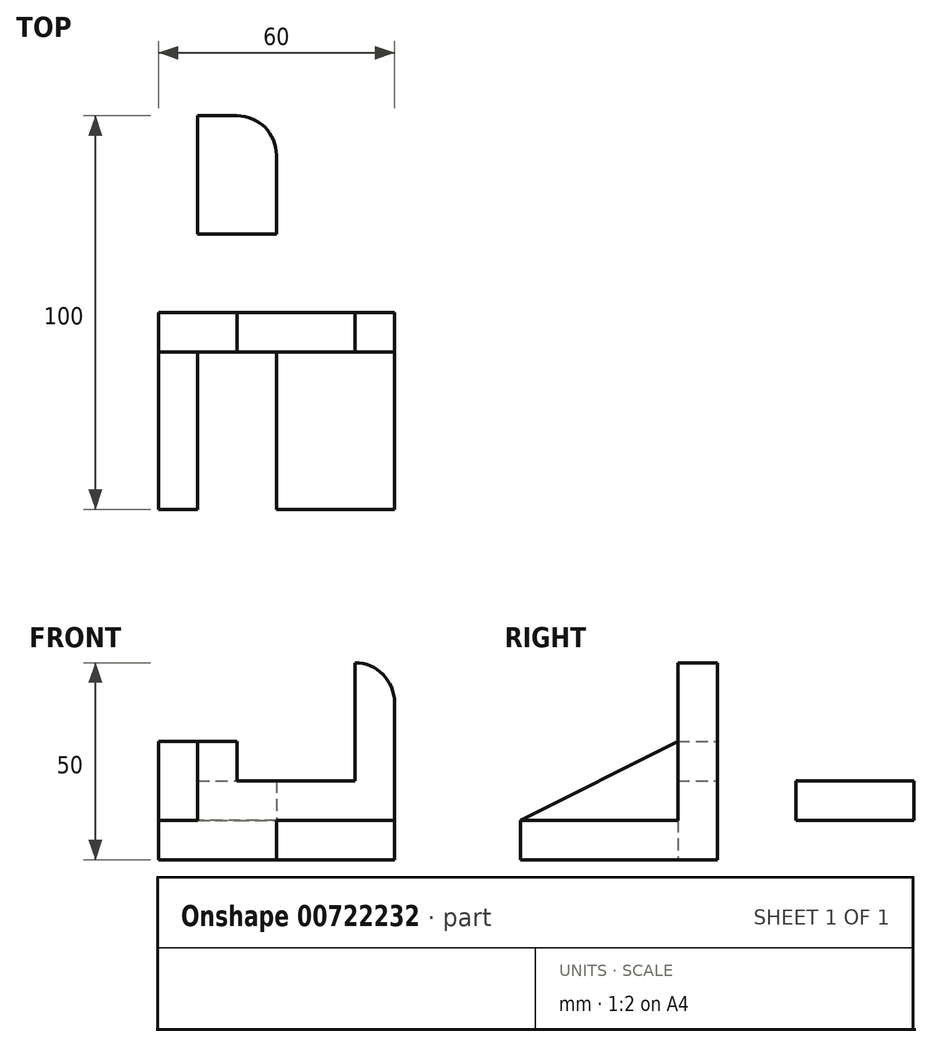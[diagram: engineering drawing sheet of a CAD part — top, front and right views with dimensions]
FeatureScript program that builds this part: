
annotation { "Feature Type Name" : "Feature", "Feature Type Description" : "" }
export const myFeature = defineFeature(function(context is Context, id is Id, definition is map)
    precondition{}
    {
        {
            var Q0;
            Q0=qCreatedBy(makeId("Front.planeOp"),FACE);
            var sketch = newSketch(context, id + "F0", { "sketchPlane" : qUnion([Q0])});
            skLineSegment(sketch, "E0", {"start": v(0, 0) * mm, "end": v(60, 0) * mm});
            skLineSegment(sketch, "E1", {"start": v(0, 0) * mm, "end": v(0, 10) * mm});
            skLineSegment(sketch, "E2", {"start": v(30, 0) * mm, "end": v(60, 0) * mm});
            skLineSegment(sketch, "E3", {"start": v(60, 10) * mm, "end": v(60, 0) * mm});
            skLineSegment(sketch, "E4", {"start": v(0, 10) * mm, "end": v(60, 10) * mm});
            skLineSegment(sketch, "E5", {"start": v(30, 10) * mm, "end": v(30, 0) * mm});
            skLineSegment(sketch, "E6", {"start": v(0, 30) * mm, "end": v(0, 10) * mm});
            skLineSegment(sketch, "E7", {"start": v(0, 30) * mm, "end": v(10, 30) * mm});
            skLineSegment(sketch, "E8", {"start": v(10, 10) * mm, "end": v(10, 30) * mm});
            skLineSegment(sketch, "E9", {"start": v(20, 30) * mm, "end": v(10, 30) * mm});
            skLineSegment(sketch, "E10", {"start": v(20, 20) * mm, "end": v(20, 30) * mm});
            skLineSegment(sketch, "E11", {"start": v(20, 20) * mm, "end": v(50, 20) * mm});
            skLineSegment(sketch, "E12", {"start": v(60, 40) * mm, "end": v(60, 10) * mm});
            skLineSegment(sketch, "E13", {"start": v(50, 50) * mm, "end": v(50, 50) * mm});
            skLineSegment(sketch, "E14", {"start": v(50, 20) * mm, "end": v(50, 50) * mm});
            skPoint(sketch, "E15.visualSharp", {"position": v(60, 50) * mm});
            skArc(sketch, "E15.filletArc", {"start": v(60, 40) * mm, "mid": v(57.07, 47.07) * mm, "end": v(50, 50) * mm});
            skSolve(sketch);
        }
        {
            var Q0;
            {var subQ0=sQuery(id+"F0.wireOp",EDGE,"E6");Q0=makeQuery(id+"F0.imprint","IMPRINT",FACE,{"disambiguationData":[TD([[makeQuery(id+"F0.imprint","IMPRINT",EDGE,{"derivedFrom":subQ0}),1.0]])]});}
            var Q1;
            Q1=makeQuery(id+"F0.imprint","IMPRINT",FACE,{"disambiguationData":[TD([[makeQuery(id+"F0.imprint","IMPRINT",EDGE,{"derivedFrom":sQuery(id+"F0.wireOp",EDGE,"E0")}),1.0]])]});
            extrude(context, id + "F1", {"entities" : qUnion([Q0, Q1]), "depth" : 50 * mm, "offsetDistance" : 25 * mm});
        }
        {
            var Q0;
            Q0 = qSketchRegion(id + "F0", true);
            extrude(context, id + "F2", {"entities" : qUnion([Q0]), "operationType" : NewBodyOperationType.ADD, "depth" : 10 * mm, "offsetDistance" : 25 * mm});
        }
        {
            var Q0;
            Q0=makeQuery(id+"F2.opExtrude","CAP_FACE",FACE,{"disambiguationData":[OSD([sQuery(id+"F0.wireOp",EDGE,"E0"),sQuery(id+"F0.wireOp",EDGE,"E1"),sQuery(id+"F0.wireOp",EDGE,"E2"),sQuery(id+"F0.wireOp",EDGE,"E3"),sQuery(id+"F0.wireOp",EDGE,"E6"),sQuery(id+"F0.wireOp",EDGE,"E7"),sQuery(id+"F0.wireOp",EDGE,"E9"),sQuery(id+"F0.wireOp",EDGE,"E10"),sQuery(id+"F0.wireOp",EDGE,"E11"),sQuery(id+"F0.wireOp",EDGE,"E12"),sQuery(id+"F0.wireOp",EDGE,"E14"),sQuery(id+"F0.wireOp",EDGE,"E15.filletArc")])],"isStart":false});
            var sketch = newSketch(context, id + "F3", { "sketchPlane" : qUnion([Q0])});
            skLineSegment(sketch, "E16", {"start": v(30, 10) * mm, "end": v(60, 10) * mm});
            skLineSegment(sketch, "E17", {"start": v(60, 10) * mm, "end": v(30, 10) * mm});
            skLineSegment(sketch, "E18", {"start": v(30, 10) * mm, "end": v(30, 0) * mm});
            skLineSegment(sketch, "E19", {"start": v(30, 0) * mm, "end": v(60, 0) * mm});
            skLineSegment(sketch, "E20", {"start": v(60, 0) * mm, "end": v(60, 10) * mm});
            skSolve(sketch);
        }
        {
            var Q0;
            Q0=makeQuery(id+"FsUGWriKy9odvux_1.boolean.opBoolean","MERGE",FACE,{"derivedFrom":[makeQuery(id+"F1.opExtrude","SWEPT_FACE",FACE,{"disambiguationData":[OSD([sQuery(id+"F0.wireOp",EDGE,"E4")])]}),makeQuery(id+"FsUGWriKy9odvux_1.opExtrude","SWEPT_FACE",FACE,{"disambiguationData":[OSD([sQuery(id+"F3.wireOp",EDGE,"E17")])]})]});
            var sketch = newSketch(context, id + "F4", { "sketchPlane" : qUnion([Q0])});
            skLineSegment(sketch, "E21", {"start": v(60, -10) * mm, "end": v(60, -10) * mm});
            skLineSegment(sketch, "E22", {"start": v(50, -20) * mm, "end": v(30, -20) * mm});
            skLineSegment(sketch, "E23", {"start": v(30, -20) * mm, "end": v(30, -10) * mm});
            skPoint(sketch, "E23.endSnap0", {"position": v(20, -10) * mm});
            skLineSegment(sketch, "E24", {"start": v(30, -10) * mm, "end": v(60, -10) * mm});
            skPoint(sketch, "E25.visualSharp", {"position": v(60, -20) * mm});
            skArc(sketch, "E25.filletArc", {"start": v(50, -20) * mm, "mid": v(57.07, -17.07) * mm, "end": v(60, -10) * mm});
            skSolve(sketch);
        }
        {
            var Q0;
            Q0=makeQuery(id+"F4.imprint","IMPRINT",FACE,{"disambiguationData":[TD([[makeQuery(id+"F4.imprint","IMPRINT",EDGE,{"derivedFrom":sQuery(id+"F4.wireOp",EDGE,"E22")}),-1.0]])]});
            extrude(context, id + "F5", {"entities" : qUnion([Q0]), "operationType" : NewBodyOperationType.ADD, "oppositeDirection" : true, "depth" : 10 * mm, "offsetDistance" : 25 * mm});
        }
        {
            var Q0;
            Q0=makeQuery(id+"F5.boolean.opBoolean","MERGE",FACE,{"derivedFrom":[makeQuery(id+"F1.opExtrude","SWEPT_FACE",FACE,{"disambiguationData":[OSD([sQuery(id+"F0.wireOp",EDGE,"E4")])]}),makeQuery(id+"F5.opExtrude","CAP_FACE",FACE,{"disambiguationData":[OSD([sQuery(id+"F4.wireOp",EDGE,"E22"),sQuery(id+"F4.wireOp",EDGE,"E23"),sQuery(id+"F4.wireOp",EDGE,"E24"),sQuery(id+"F4.wireOp",EDGE,"E25.filletArc")])],"isStart":true})]});
            var sketch = newSketch(context, id + "F6", { "sketchPlane" : qUnion([Q0])});
            skLineSegment(sketch, "E26", {"start": v(10, -50) * mm, "end": v(20, -50) * mm});
            skLineSegment(sketch, "E27", {"start": v(30, -40) * mm, "end": v(30, -20) * mm});
            skLineSegment(sketch, "E28", {"start": v(30, -20) * mm, "end": v(10, -20) * mm});
            skLineSegment(sketch, "E29", {"start": v(10, -20) * mm, "end": v(10, -50) * mm});
            skPoint(sketch, "E30.visualSharp", {"position": v(30, -50) * mm});
            skArc(sketch, "E30.filletArc", {"start": v(20, -50) * mm, "mid": v(27.07, -47.07) * mm, "end": v(30, -40) * mm});
            skLineSegment(sketch, "E31", {"start": v(20, -50) * mm, "end": v(30, -50) * mm});
            skLineSegment(sketch, "E32", {"start": v(30, -40) * mm, "end": v(30, -50) * mm});
            skSolve(sketch);
        }
        {
            var Q0;
            Q0 = qSketchRegion(id + "F6", true);
            extrude(context, id + "F7", {"entities" : qUnion([Q0]), "operationType" : NewBodyOperationType.ADD, "oppositeDirection" : true, "depth" : 10 * mm, "offsetDistance" : 25 * mm});
        }
        {
            var Q0;
            Q0=makeQuery(id+"F5.boolean.opBoolean","MERGE",FACE,{"derivedFrom":[makeQuery(id+"F1.opExtrude","SWEPT_FACE",FACE,{"disambiguationData":[OSD([sQuery(id+"F0.wireOp",EDGE,"E4")])]}),makeQuery(id+"F5.opExtrude","CAP_FACE",FACE,{"disambiguationData":[OSD([sQuery(id+"F4.wireOp",EDGE,"E22"),sQuery(id+"F4.wireOp",EDGE,"E23"),sQuery(id+"F4.wireOp",EDGE,"E24"),sQuery(id+"F4.wireOp",EDGE,"E25.filletArc")])],"isStart":true})]});
            var sketch = newSketch(context, id + "F8", { "sketchPlane" : qUnion([Q0])});
            skLineSegment(sketch, "E33", {"start": v(30, -50) * mm, "end": v(20, -50) * mm});
            skLineSegment(sketch, "E34", {"start": v(30, -40) * mm, "end": v(30, -50) * mm});
            skArc(sketch, "E35", {"start": v(20, -50) * mm, "mid": v(27.07, -47.07) * mm, "end": v(30, -40) * mm});
            skSolve(sketch);
        }
        {
            var Q0;
            Q0 = qSketchRegion(id + "F8", true);
            extrude(context, id + "F9", {"entities" : qUnion([Q0]), "operationType" : NewBodyOperationType.REMOVE, "oppositeDirection" : true, "depth" : 25 * mm, "offsetDistance" : 25 * mm});
        }
        {
            var Q0;
            Q0=makeQuery(id+"F1.opExtrude","SWEPT_FACE",FACE,{"disambiguationData":[OSD([sQuery(id+"F0.wireOp",EDGE,"E8")])]});
            var sketch = newSketch(context, id + "F10", { "sketchPlane" : qUnion([Q0])});
            skLineSegment(sketch, "E36", {"start": v(-10, 30) * mm, "end": v(-50, 10) * mm});
            skLineSegment(sketch, "E37", {"start": v(-50, 10) * mm, "end": v(-50, 30) * mm});
            skLineSegment(sketch, "E38", {"start": v(-50, 30) * mm, "end": v(-10, 30) * mm});
            skSolve(sketch);
        }
        {
            var Q0;
            Q0=makeQuery(id+"F10.imprint","IMPRINT",FACE,{"disambiguationData":[TD([[makeQuery(id+"F10.imprint","IMPRINT",EDGE,{"derivedFrom":sQuery(id+"F10.wireOp",EDGE,"E36")}),-1.0]])]});
            extrude(context, id + "F11", {"entities" : qUnion([Q0]), "operationType" : NewBodyOperationType.REMOVE, "oppositeDirection" : true, "depth" : 25 * mm, "offsetDistance" : 25 * mm});
        }
    });
